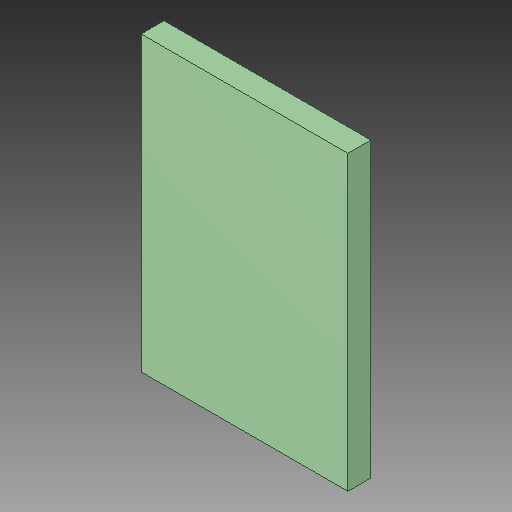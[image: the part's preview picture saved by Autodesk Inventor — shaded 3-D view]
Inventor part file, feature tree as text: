
AUTODESK INVENTOR PART (.ipt)
format: ipt  version: 2019 (Build 230136000, 136)  size: 86,016 bytes
history: native  units: in
note: dims shown in document units (in); Inventor stores cm internally (conversion verified against a paired STEP export)
features: extrude x1, other x1
ambient origin geometry x8: Origin, YZ Plane, XZ Plane, XY Plane, X Axis, Y Axis, Z Axis, Center Point
bodies: Solid1 (feature_tree)
feature tree (2):
  extrude  "Extrusion1"  Depth=0.0394in TaperAngle=0.0deg
  other  "REG-AMS1117-3P, REG-AMS1117-3P-3_3V_25"
